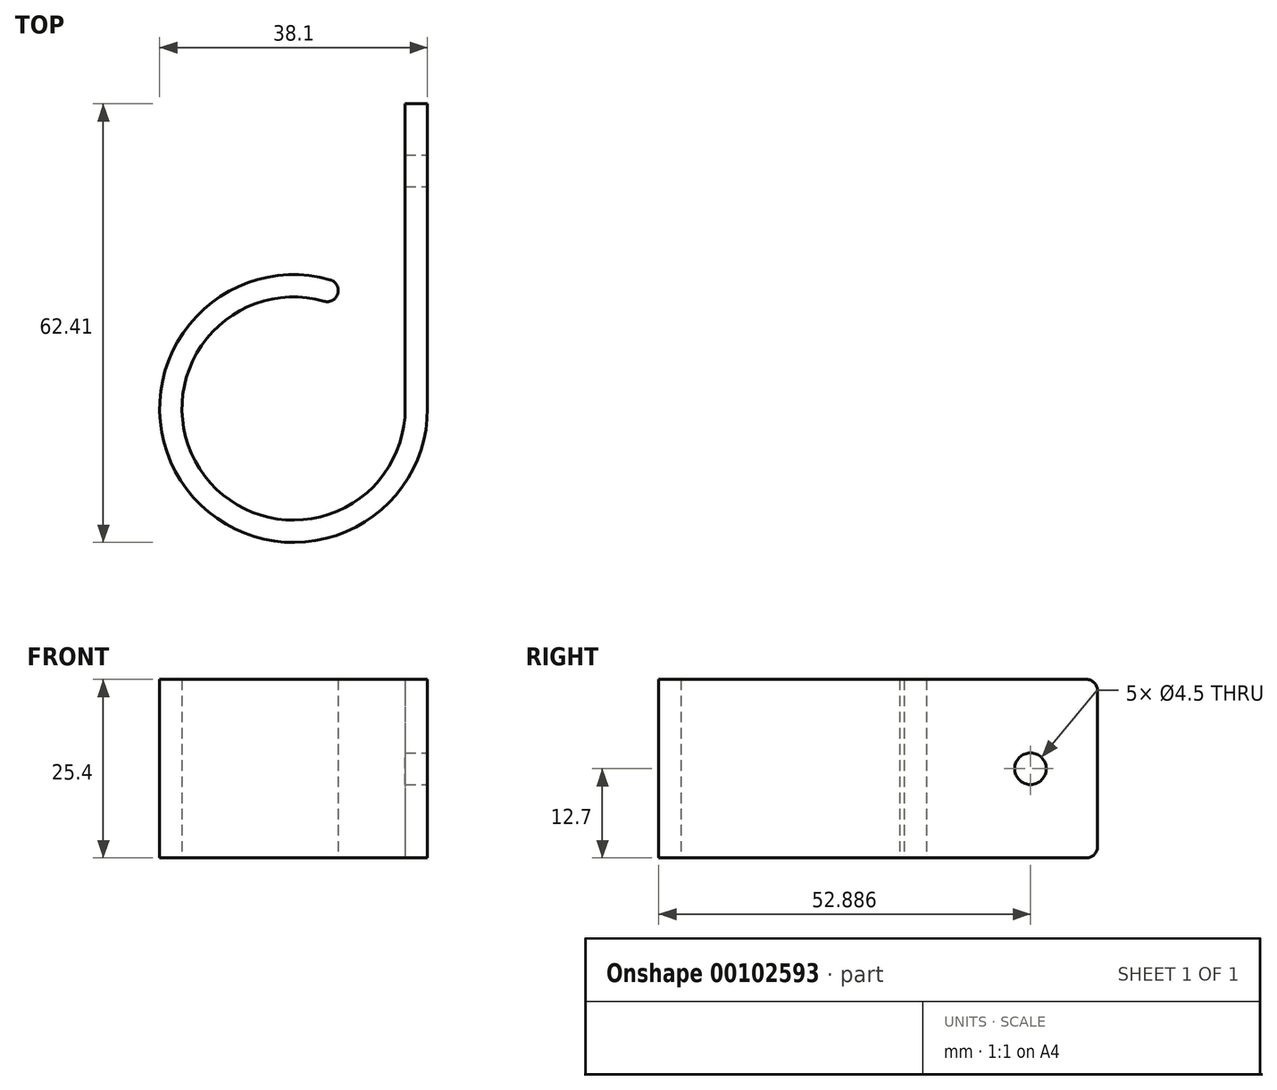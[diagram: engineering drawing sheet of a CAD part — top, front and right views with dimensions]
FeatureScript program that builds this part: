
annotation { "Feature Type Name" : "Feature", "Feature Type Description" : "" }
export const myFeature = defineFeature(function(context is Context, id is Id, definition is map)
    precondition{}
    {
        {
            var Q0;
            Q0=qCreatedBy(makeId("Top.planeOp"),FACE);
            var sketch = newSketch(context, id + "F0", { "sketchPlane" : qUnion([Q0])});
            skLineSegment(sketch, "E0", {"start": v(0, 0) * mm, "end": v(0, 43.36) * mm});
            skLineSegment(sketch, "E1", {"start": v(0, 43.36) * mm, "end": v(3.17, 43.36) * mm});
            skLineSegment(sketch, "E2", {"start": v(3.17, 43.36) * mm, "end": v(3.18, 0) * mm});
            skArc(sketch, "E3", {"start": v(-9.53, 17.96) * mm, "mid": v(-31.43, -11) * mm, "end": v(3.17, 0) * mm});
            skLineSegment(sketch, "E4", {"start": v(-9.53, 17.96) * mm, "end": v(-9.53, 14.55) * mm});
            skArc(sketch, "E5.0", {"start": v(-9.53, 14.55) * mm, "mid": v(-29.16, -8.7) * mm, "end": v(0, 0) * mm});
            skSolve(sketch);
        }
        {
            var Q0;
            Q0=makeQuery(id+"F0.imprint","IMPRINT",FACE,{"disambiguationData":[TD([[makeQuery(id+"F0.imprint","IMPRINT",EDGE,{"derivedFrom":sQuery(id+"F0.wireOp",EDGE,"E0")}),-1.0]])]});
            extrude(context, id + "F1", {"entities" : qUnion([Q0]), "depth" : 25.4 * mm, "symmetric" : true});
        }
        {
            var Q0;
            Q0=makeQuery(id+"F1.opExtrude","SWEPT_EDGE",EDGE,{"disambiguationData":[OSD([sQuery(id+"F0.wireOp",EDGE,"E4"),sQuery(id+"F0.wireOp",EDGE,"E5.0")])]});
            var Q1;
            Q1=makeQuery(id+"F1.opExtrude","SWEPT_EDGE",EDGE,{"disambiguationData":[OSD([sQuery(id+"F0.wireOp",EDGE,"E3"),sQuery(id+"F0.wireOp",EDGE,"E4")])]});
            fillet(context, id + "F2", {"entities" : qUnion([Q0, Q1]), "radius" : 1.59 * mm, "tangentPropagation" : true, "allowEdgeOverflow" : false});
        }
        {
            var Q0;
            Q0=makeQuery(id+"F1.opExtrude","CAP_EDGE",EDGE,{"disambiguationData":[OSD([sQuery(id+"F0.wireOp",EDGE,"E1")])],"isStart":false});
            var Q1;
            Q1=makeQuery(id+"F1.opExtrude","CAP_EDGE",EDGE,{"disambiguationData":[OSD([sQuery(id+"F0.wireOp",EDGE,"E1")])],"isStart":true});
            fillet(context, id + "F3", {"entities" : qUnion([Q0, Q1]), "radius" : 1.59 * mm, "tangentPropagation" : true, "allowEdgeOverflow" : false});
        }
        {
            var Q0;
            Q0=qCreatedBy(makeId("Right.planeOp"),FACE);
            var sketch = newSketch(context, id + "F4", { "sketchPlane" : qUnion([Q0])});
            skPoint(sketch, "E6", {"position": v(33.84, 0) * mm});
            skSolve(sketch);
        }
        {
            var Q0;
            Q0=sQuery(id+"F4.wireOp",VERTEX,"E6");
            var Q1;
            Q1=makeQuery(id+"F1.opExtrude","SWEPT_BODY",BODY,{"disambiguationData":[OSD([sQuery(id+"F0.wireOp",EDGE,"E0"),sQuery(id+"F0.wireOp",EDGE,"E1"),sQuery(id+"F0.wireOp",EDGE,"E2"),sQuery(id+"F0.wireOp",EDGE,"E3"),sQuery(id+"F0.wireOp",EDGE,"E4"),sQuery(id+"F0.wireOp",EDGE,"E5.0")])]});
            hole(context, id + "F5", {"style" : HoleStyle.SIMPLE, "endStyle" : HoleEndStyle.THROUGH, "oppositeDirection" : true, "standardTappedOrClearance" : lookupTablePath({ "standard" : "ANSI", "fit" : "Normal (ASME)", "size" : "#8", "type" : "Clearance" }), "standardBlindInLast" : lookupTablePath({ "fit" : "Free", "standard" : "ANSI", "size" : "#8", "type" : "Clearance" }), "holeDiameter" : 4.5 * mm, "locations" : qUnion([Q0]), "scope" : qUnion([Q1]), "isTappedThrough" : true, "startStyle" : HoleStartStyle.SKETCH});
        }
    });
